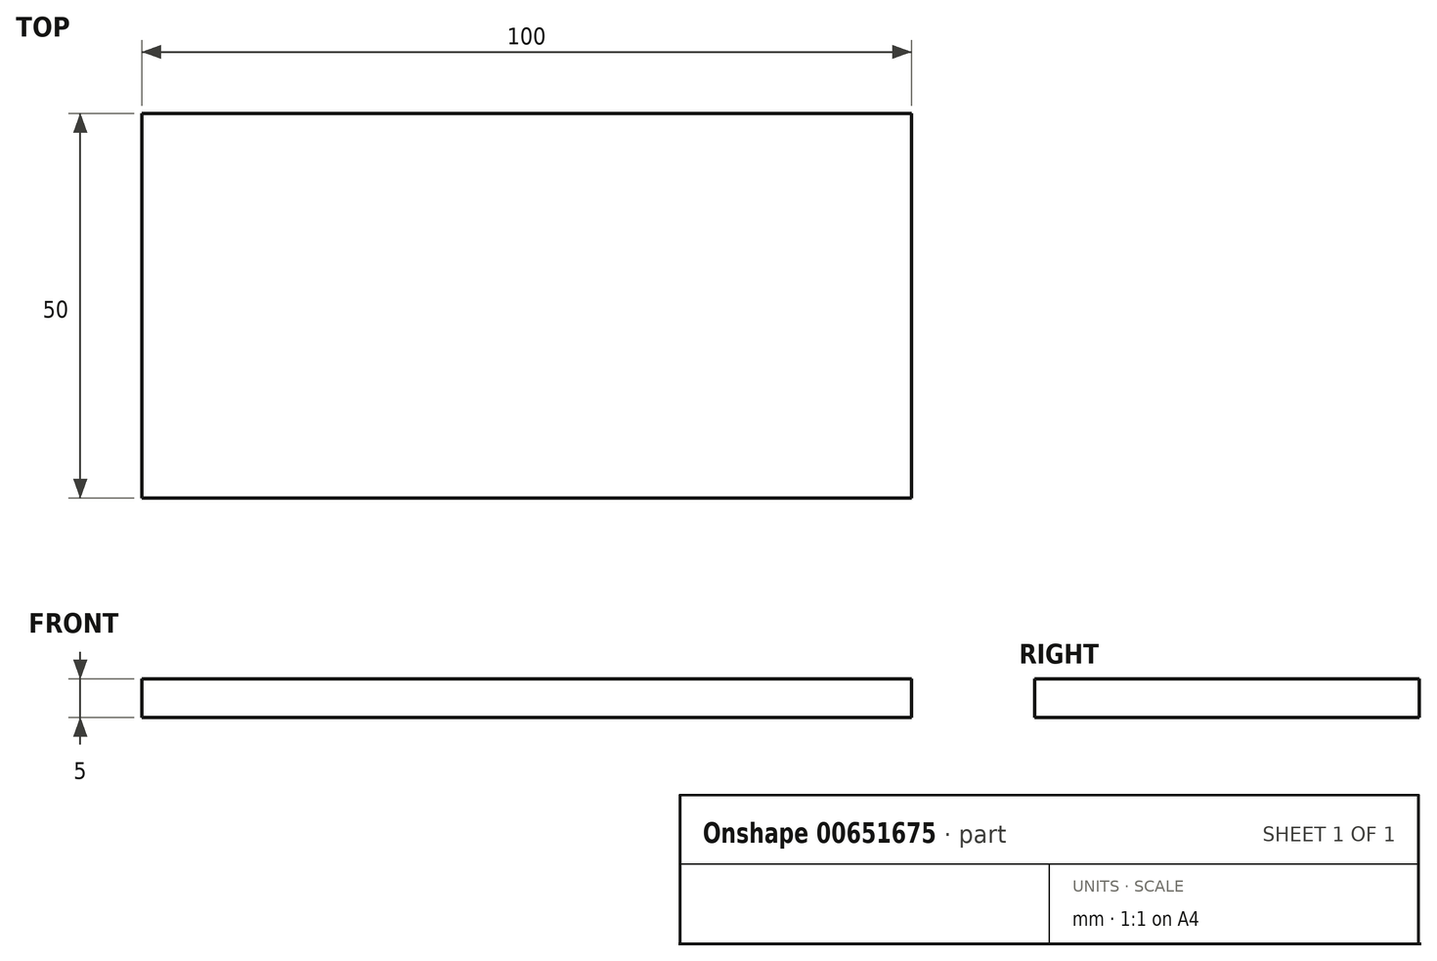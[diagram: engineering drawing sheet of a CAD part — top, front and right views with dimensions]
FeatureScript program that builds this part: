
annotation { "Feature Type Name" : "Feature", "Feature Type Description" : "" }
export const myFeature = defineFeature(function(context is Context, id is Id, definition is map)
    precondition{}
    {
        {
            var Q0;
            Q0=qCreatedBy(makeId("Top.planeOp"),FACE);
            var sketch = newSketch(context, id + "F0", { "sketchPlane" : qUnion([Q0])});
            skLineSegment(sketch, "E0.bottom", {"start": v(0, 0) * mm, "end": v(-100, 0) * mm});
            skLineSegment(sketch, "E0.top", {"start": v(0, 50) * mm, "end": v(-100, 50) * mm});
            skLineSegment(sketch, "E0.left", {"start": v(0, 0) * mm, "end": v(0, 50) * mm});
            skLineSegment(sketch, "E0.right", {"start": v(-100, 0) * mm, "end": v(-100, 50) * mm});
            skSolve(sketch);
        }
        {
            var Q0;
            Q0 = qSketchRegion(id + "F0", true);
            extrude(context, id + "F1", {"entities" : qUnion([Q0]), "depth" : 5 * mm, "offsetDistance" : 25 * mm});
        }
    });
